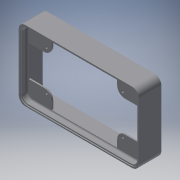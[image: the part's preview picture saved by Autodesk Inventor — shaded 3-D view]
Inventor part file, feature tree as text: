
AUTODESK INVENTOR PART (.ipt)
format: ipt  version: 2018 (Build 220112000, 112)  size: 217,088 bytes
history: native  units: in
note: dims shown in document units (in); Inventor stores cm internally (conversion verified against a paired STEP export)
features: reference x6, extrude x4, sketch x4, projected_geometry x3, other x3, fillet x1
ambient origin geometry x8: Origin, YZ Plane, XZ Plane, XY Plane, X Axis, Y Axis, Z Axis, Center Point
bodies: Solid1 (feature_tree)
feature tree (21):
  extrude  "Extrusion1"  Depth=0.1181in
  extrude  "Extrusion2"  Depth=0.1181in
  extrude  "Extrusion3"  Depth=0.4331in
  fillet  "Fillet1"  Radius=0.4724in
  extrude  "Extrusion4"  Depth=0.0591in TaperAngle=0.0deg
  sketch  "Sketch1"  dims[d0=0.1181in d1=0.1181in]
  reference  "Reference1"
  sketch  "Sketch2"  dims[d2=0.1181in d3=0.1181in]
  projected_geometry  "Projected Loop1"
  reference  "Reference2"
  sketch  "Sketch3"  dims[d4=0.4331in d5=0.4331in d6=0.4724in d7=0.0in]
  projected_geometry  "Projected Loop2"
  sketch  "Sketch5"  dims[d8=0.0394in d9=0.0591in d10=0.0in d11=0.0787in d12=0.3898in d13=0.0in d14=0.125in d38=0.15in d39=0.15in d40=0.15in d41=0.15in d51=0.5in d52=1.0in d53=1.5in d54=1.0in d55=0.0in]
  projected_geometry  "Projected Loop4"
  reference  "Reference15"
  reference  "Reference16"
  reference  "Reference17"
  reference  "Reference18"
  other  "<userpath>\Desktop\LocalGit\seniorproject\hardware\mechanical\Hub\Hub Assembly.iam"
  other  "Hub Assembly.iam"
  other  "Touchscreen:1"
